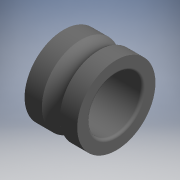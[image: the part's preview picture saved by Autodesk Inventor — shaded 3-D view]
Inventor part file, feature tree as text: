
AUTODESK INVENTOR PART (.ipt)
format: ipt  version: 2017.3 (Build 213256000, 256)  size: 148,480 bytes
history: native  units: mm (DEFAULTED — no unit token found)
features: other x63, revolve x1, sketch x1
ambient origin geometry x8: Origin, YZ Plane, XZ Plane, XY Plane, X Axis, Y Axis, Z Axis, Center Point
bodies: Solid1 (feature_tree)
feature tree (65):
  revolve  "Revolution1"  [1 undecoded]
  other  "ip_op_ir_1_1_XY"
  other  "ip_op_ir_1_1_YZ"
  other  "ip_op_ir_1_1_ZX"
  other  "ip_op_ir_1_1_X"
  other  "ip_op_ir_1_1_Y"
  other  "ip_op_ir_1_1_Z"
  other  "ip_op_ir_1_1_Center"
  other  "ip_op_ir_1_2_XY"
  other  "ip_op_ir_1_2_YZ"
  other  "ip_op_ir_1_2_ZX"
  other  "ip_op_ir_1_2_X"
  other  "ip_op_ir_1_2_Y"
  other  "ip_op_ir_1_2_Z"
  other  "ip_op_ir_1_2_Center"
  other  "ip_op_ir_1_3_XY"
  other  "ip_op_ir_1_3_YZ"
  other  "ip_op_ir_1_3_ZX"
  other  "ip_op_ir_1_3_X"
  other  "ip_op_ir_1_3_Y"
  other  "ip_op_ir_1_3_Z"
  other  "ip_op_ir_1_3_Center"
  other  "ip_op_ir_1_4_XY"
  other  "ip_op_ir_1_4_YZ"
  other  "ip_op_ir_1_4_ZX"
  other  "ip_op_ir_1_4_X"
  other  "ip_op_ir_1_4_Y"
  other  "ip_op_ir_1_4_Z"
  other  "ip_op_ir_1_4_Center"
  other  "ip_op_ir_1_5_XY"
  other  "ip_op_ir_1_5_YZ"
  other  "ip_op_ir_1_5_ZX"
  other  "ip_op_ir_1_5_X"
  other  "ip_op_ir_1_5_Y"
  other  "ip_op_ir_1_5_Z"
  other  "ip_op_ir_1_5_Center"
  other  "ip_op_ir_1_6_XY"
  other  "ip_op_ir_1_6_YZ"
  other  "ip_op_ir_1_6_ZX"
  other  "ip_op_ir_1_6_X"
  other  "ip_op_ir_1_6_Y"
  other  "ip_op_ir_1_6_Z"
  other  "ip_op_ir_1_6_Center"
  other  "ip_op_ir_1_7_XY"
  other  "ip_op_ir_1_7_YZ"
  other  "ip_op_ir_1_7_ZX"
  other  "ip_op_ir_1_7_X"
  other  "ip_op_ir_1_7_Y"
  other  "ip_op_ir_1_7_Z"
  other  "ip_op_ir_1_7_Center"
  other  "ip_op_ir_1_8_XY"
  other  "ip_op_ir_1_8_YZ"
  other  "ip_op_ir_1_8_ZX"
  other  "ip_op_ir_1_8_X"
  other  "ip_op_ir_1_8_Y"
  other  "ip_op_ir_1_8_Z"
  other  "ip_op_ir_1_8_Center"
  other  "ip_op_ir_1a_XY"
  other  "ip_op_ir_1a_YZ"
  other  "ip_op_ir_1a_ZX"
  other  "ip_op_ir_1a_X"
  other  "ip_op_ir_1a_Y"
  other  "ip_op_ir_1a_Z"
  other  "ip_op_ir_1a_Center"
  sketch  "Sketch_1"  dims[d0=360.0deg d1=0.0mm]
note: 1 required parameter value undecoded (feature->parameter linkage not recoverable at this tier; creation-order binding heuristic only, values carry confidence <= 0.55)
